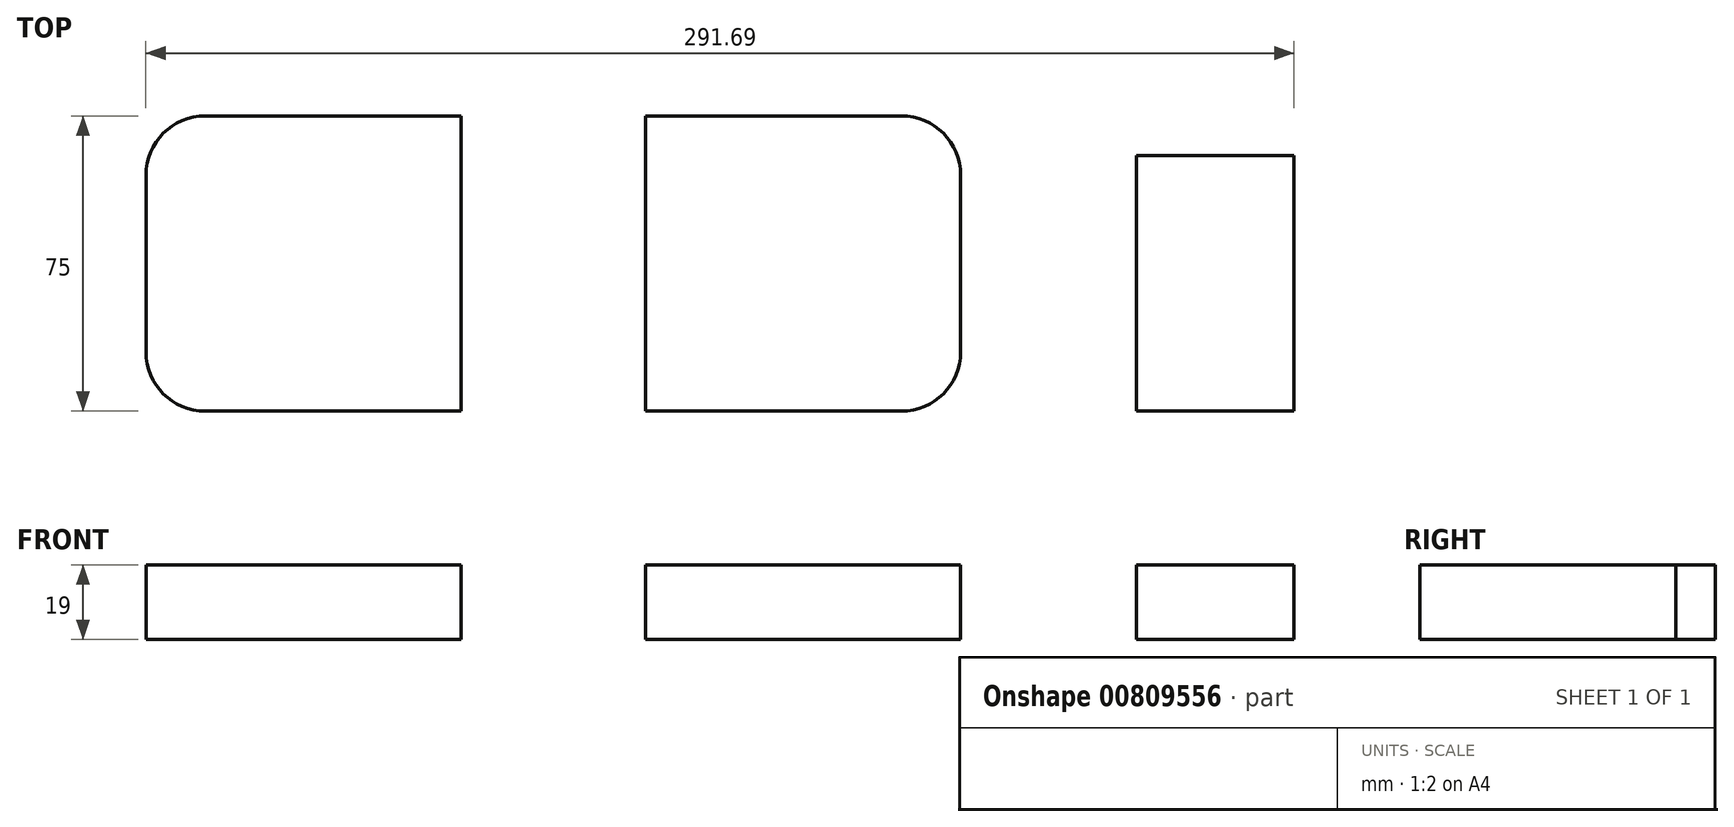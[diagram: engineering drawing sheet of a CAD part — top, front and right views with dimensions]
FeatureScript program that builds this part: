
annotation { "Feature Type Name" : "Feature", "Feature Type Description" : "" }
export const myFeature = defineFeature(function(context is Context, id is Id, definition is map)
    precondition{}
    {
        {
            var Q0;
            Q0=qCreatedBy(makeId("Top.planeOp"),FACE);
            var sketch = newSketch(context, id + "F0", { "sketchPlane" : qUnion([Q0])});
            skLineSegment(sketch, "E0.bottom", {"start": v(-169.77, 14.8) * mm, "end": v(-104.77, 14.8) * mm});
            skLineSegment(sketch, "E0.top", {"start": v(-169.77, -60.2) * mm, "end": v(-104.77, -60.2) * mm});
            skLineSegment(sketch, "E0.left", {"start": v(-184.77, -0.2) * mm, "end": v(-184.77, -45.2) * mm});
            skLineSegment(sketch, "E0.right", {"start": v(-104.77, 14.8) * mm, "end": v(-104.77, -60.2) * mm});
            skPoint(sketch, "E1.firstSnap0", {"position": v(-144.77, 14.8) * mm});
            skLineSegment(sketch, "E1.bottom", {"start": v(-57.78, 14.8) * mm, "end": v(7.22, 14.8) * mm});
            skLineSegment(sketch, "E1.top", {"start": v(-57.78, -60.2) * mm, "end": v(7.22, -60.2) * mm});
            skLineSegment(sketch, "E1.left", {"start": v(-57.78, 14.8) * mm, "end": v(-57.78, -60.2) * mm});
            skLineSegment(sketch, "E1.right", {"start": v(22.22, -0.2) * mm, "end": v(22.22, -45.2) * mm});
            skLineSegment(sketch, "E2.bottom", {"start": v(66.92, -60.2) * mm, "end": v(106.92, -60.2) * mm});
            skLineSegment(sketch, "E2.top", {"start": v(66.92, 4.8) * mm, "end": v(106.92, 4.8) * mm});
            skLineSegment(sketch, "E2.left", {"start": v(66.92, -60.2) * mm, "end": v(66.92, 4.8) * mm});
            skLineSegment(sketch, "E2.right", {"start": v(106.92, -60.2) * mm, "end": v(106.92, 4.8) * mm});
            skPoint(sketch, "E3.visualSharp", {"position": v(-184.77, -60.2) * mm});
            skArc(sketch, "E3.filletArc", {"start": v(-184.77, -45.2) * mm, "mid": v(-180.37, -55.8) * mm, "end": v(-169.77, -60.2) * mm});
            skPoint(sketch, "E4.visualSharp", {"position": v(-184.77, 14.8) * mm});
            skArc(sketch, "E4.filletArc", {"start": v(-169.77, 14.8) * mm, "mid": v(-180.37, 10.4) * mm, "end": v(-184.77, -0.2) * mm});
            skPoint(sketch, "E5.visualSharp", {"position": v(22.22, 14.8) * mm});
            skArc(sketch, "E5.filletArc", {"start": v(22.22, -0.2) * mm, "mid": v(17.83, 10.4) * mm, "end": v(7.22, 14.8) * mm});
            skPoint(sketch, "E6.visualSharp", {"position": v(22.22, -60.2) * mm});
            skArc(sketch, "E6.filletArc", {"start": v(7.22, -60.2) * mm, "mid": v(17.83, -55.8) * mm, "end": v(22.22, -45.2) * mm});
            skSolve(sketch);
        }
        {
            var Q0;
            Q0 = qSketchRegion(id + "F0", true);
            extrude(context, id + "F1", {"entities" : qUnion([Q0]), "depth" : 19 * mm, "offsetDistance" : 25 * mm});
        }
    });
